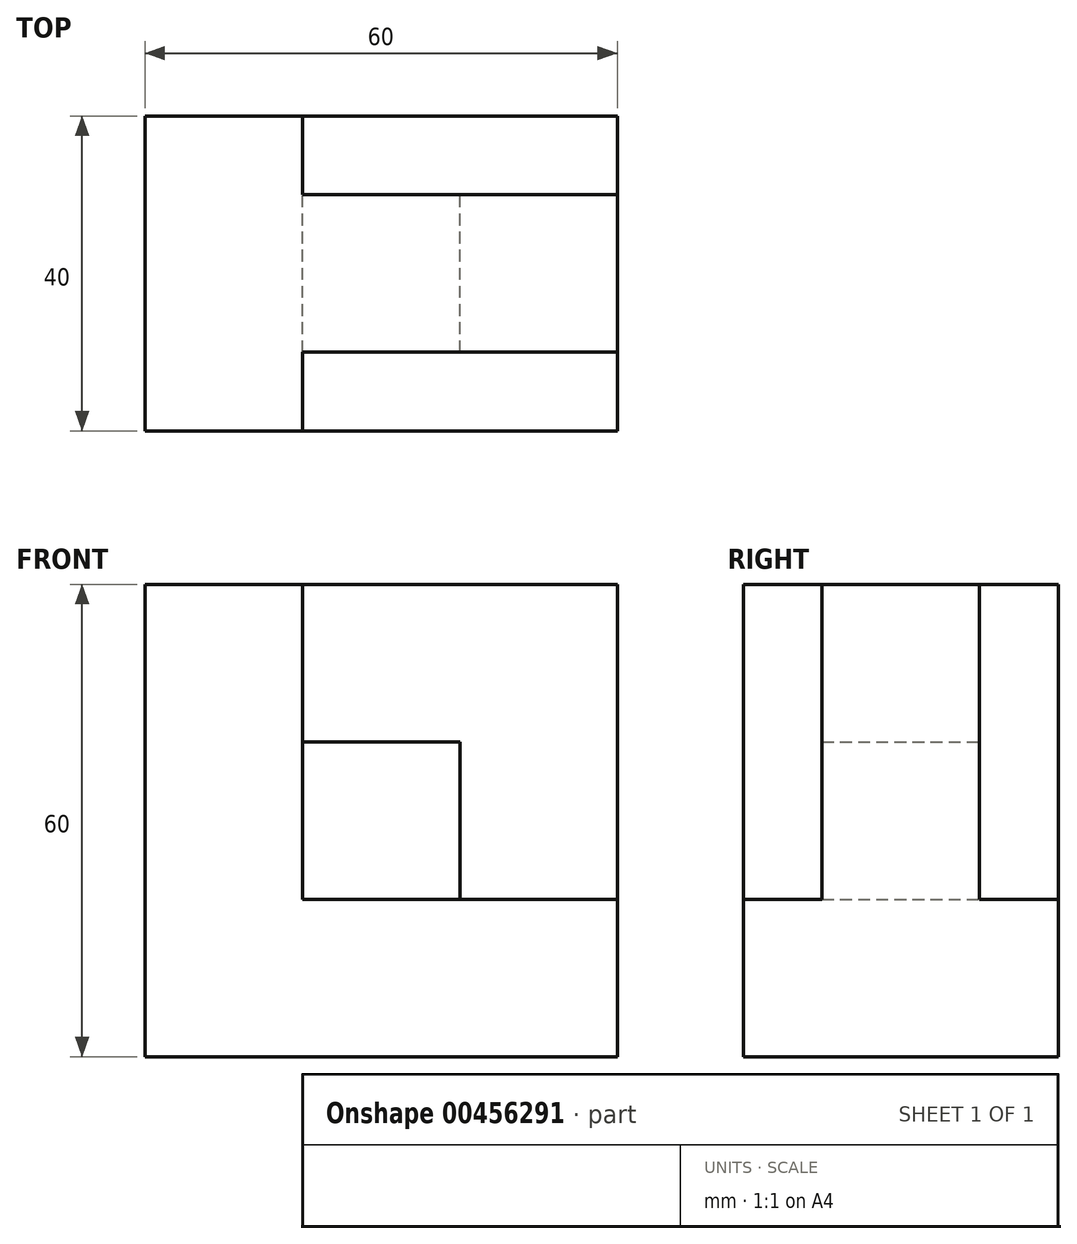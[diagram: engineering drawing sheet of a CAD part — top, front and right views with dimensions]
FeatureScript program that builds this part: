
annotation { "Feature Type Name" : "Feature", "Feature Type Description" : "" }
export const myFeature = defineFeature(function(context is Context, id is Id, definition is map)
    precondition{}
    {
        {
            var Q0;
            Q0=qCreatedBy(makeId("Front.planeOp"),FACE);
            var sketch = newSketch(context, id + "F0", { "sketchPlane" : qUnion([Q0])});
            skLineSegment(sketch, "E0", {"start": v(0, 0) * mm, "end": v(0, 60) * mm});
            skLineSegment(sketch, "E1", {"start": v(0, 60) * mm, "end": v(20, 60) * mm});
            skLineSegment(sketch, "E2", {"start": v(20, 60) * mm, "end": v(20, 20) * mm});
            skLineSegment(sketch, "E3", {"start": v(20, 20) * mm, "end": v(60, 20) * mm});
            skLineSegment(sketch, "E4", {"start": v(60, 20) * mm, "end": v(60, 0) * mm});
            skLineSegment(sketch, "E5", {"start": v(60, 0) * mm, "end": v(0, 0) * mm});
            skLineSegment(sketch, "E6", {"start": v(20, 60) * mm, "end": v(60, 60) * mm});
            skLineSegment(sketch, "E7", {"start": v(60, 60) * mm, "end": v(60, 20) * mm});
            skLineSegment(sketch, "E8", {"start": v(20, 40) * mm, "end": v(40, 40) * mm});
            skLineSegment(sketch, "E9", {"start": v(40, 40) * mm, "end": v(40, 20) * mm});
            skSolve(sketch);
        }
        {
            var Q0;
            Q0=makeQuery(id+"F0.imprint","IMPRINT",FACE,{"disambiguationData":[TD([[makeQuery(id+"F0.imprint","IMPRINT",EDGE,{"derivedFrom":sQuery(id+"F0.wireOp",EDGE,"E0")}),-1.0]])]});
            extrude(context, id + "F1", {"entities" : qUnion([Q0]), "endBound" : BoundingType.SYMMETRIC, "depth" : 40 * mm});
        }
        {
            var Q0;
            Q0=qSketchRegion(id+"F0",true);
            extrude(context, id + "F2", {"entities" : qUnion([Q0]), "operationType" : NewBodyOperationType.ADD, "endBound" : BoundingType.SYMMETRIC, "depth" : 20 * mm});
        }
    });
